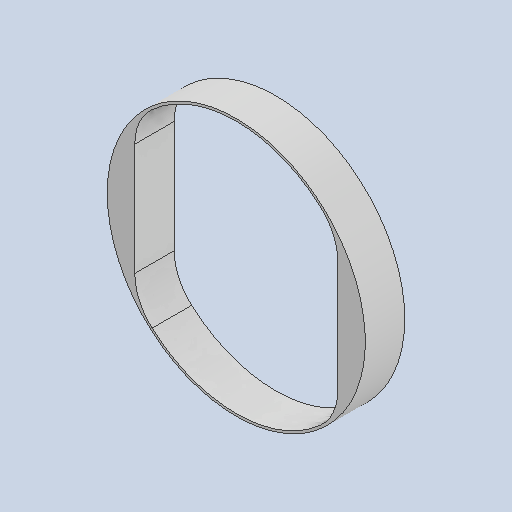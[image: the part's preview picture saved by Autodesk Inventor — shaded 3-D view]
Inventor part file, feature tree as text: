
AUTODESK INVENTOR PART (.ipt)
format: ipt  version: 2022 (Build 260153000, 153)  size: 113,664 bytes
history: native  units: in
note: dims shown in document units (in); Inventor stores cm internally (conversion verified against a paired STEP export)
features: other x3, sketch x1, plane x1
ambient origin geometry x8: Origin, YZ Plane, XZ Plane, XY Plane, X Axis, Y Axis, Z Axis, Center Point
bodies: Solid1 (feature_tree)
feature tree (5):
  other  "encoderring_MIR.ipt"
  other  "Solid1::encoderring_MIR.ipt"
  other  "TaggingFeature1"
  sketch  "Sketch1"  dims[d0=0.3937in]
  plane  "Work Plane1"
